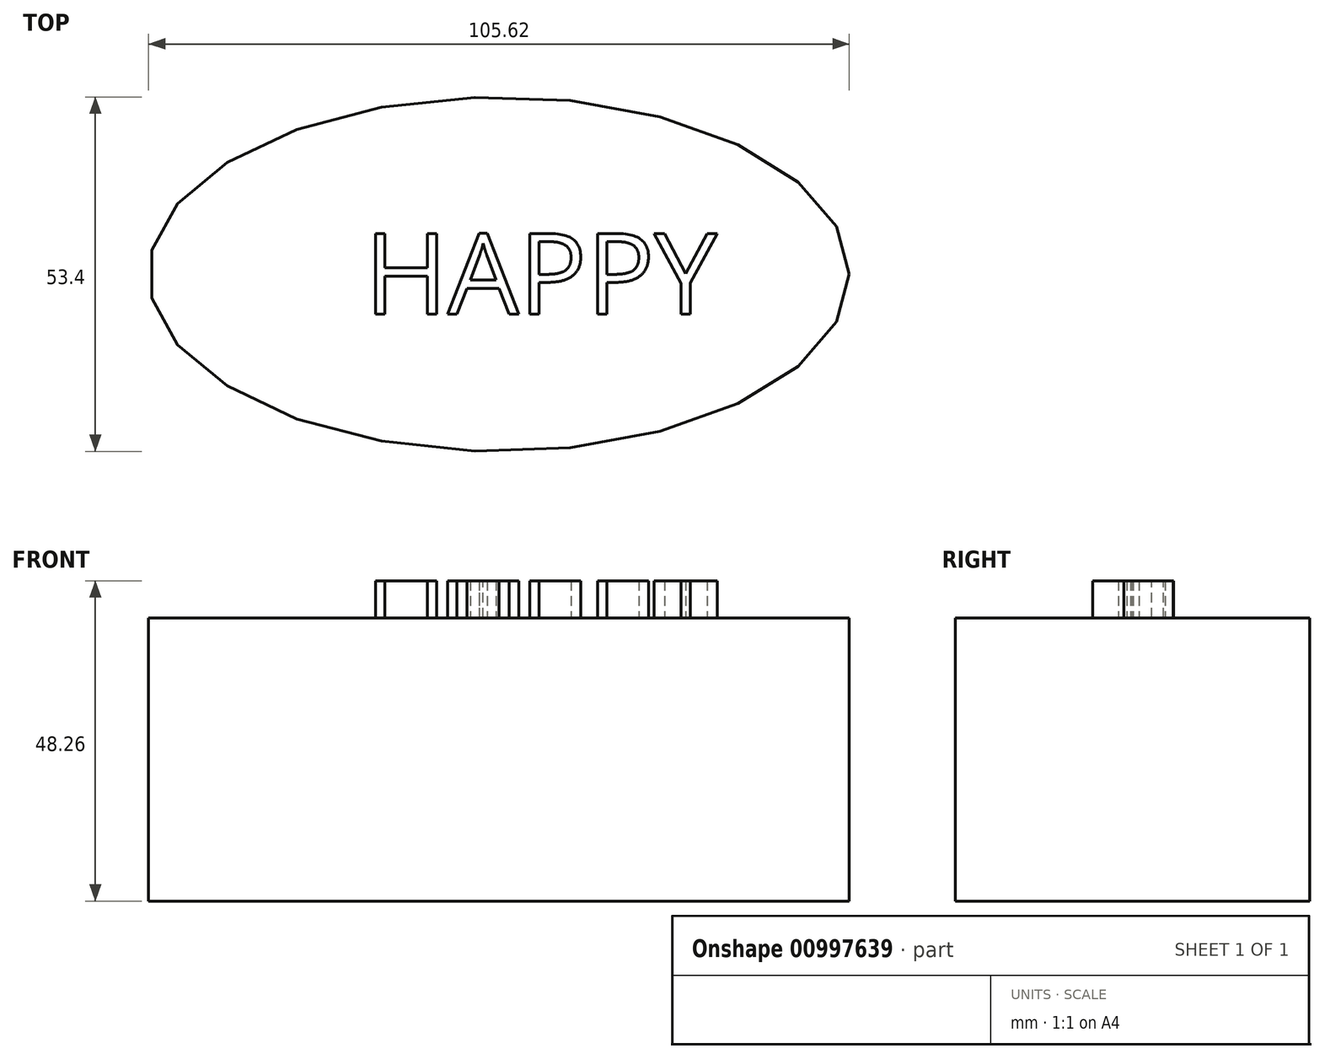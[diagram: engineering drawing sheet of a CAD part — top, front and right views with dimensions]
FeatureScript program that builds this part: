
annotation { "Feature Type Name" : "Feature", "Feature Type Description" : "" }
export const myFeature = defineFeature(function(context is Context, id is Id, definition is map)
    precondition{}
    {
        {
            var Q0;
            Q0=qCreatedBy(makeId("Top.planeOp"),FACE);
            var sketch = newSketch(context, id + "F0", { "sketchPlane" : qUnion([Q0])});
            skEllipse(sketch, "E0", {"center": v(-17.55, 0) * mm, "majorRadius": 52.81 * mm, "minorRadius": 26.7 * mm, "majorAxis": v(1, 0)});
            skSolve(sketch);
        }
        {
            var Q0;
            Q0 = qSketchRegion(id + "F0", true);
            extrude(context, id + "F1", {"entities" : qUnion([Q0]), "depth" : 42.67 * mm, "offsetDistance" : 25.4 * mm});
        }
        {
            var Q0;
            Q0=makeQuery(id+"F1.opExtrude","CAP_FACE",FACE,{"disambiguationData":[OSD([sQuery(id+"F0.wireOp",EDGE,"E0")])],"isStart":false});
            var sketch = newSketch(context, id + "F2", { "sketchPlane" : qUnion([Q0])});
            skText(sketch, "E1", { "text": "HAPPY", "fontName": "OpenSans-Regular.ttf"});
            const initialGuessF2  = {"E1": [-0.0378, -0.006, 1, 0, 0.01221]};
            skSetInitialGuess(sketch, initialGuessF2);
            skSolve(sketch);
        }
        {
            var Q0;
            Q0 = qSketchRegion(id + "F2", true);
            extrude(context, id + "F3", {"entities" : qUnion([Q0]), "operationType" : NewBodyOperationType.ADD, "depth" : 5.6 * mm, "offsetDistance" : 25.4 * mm});
        }
    });
